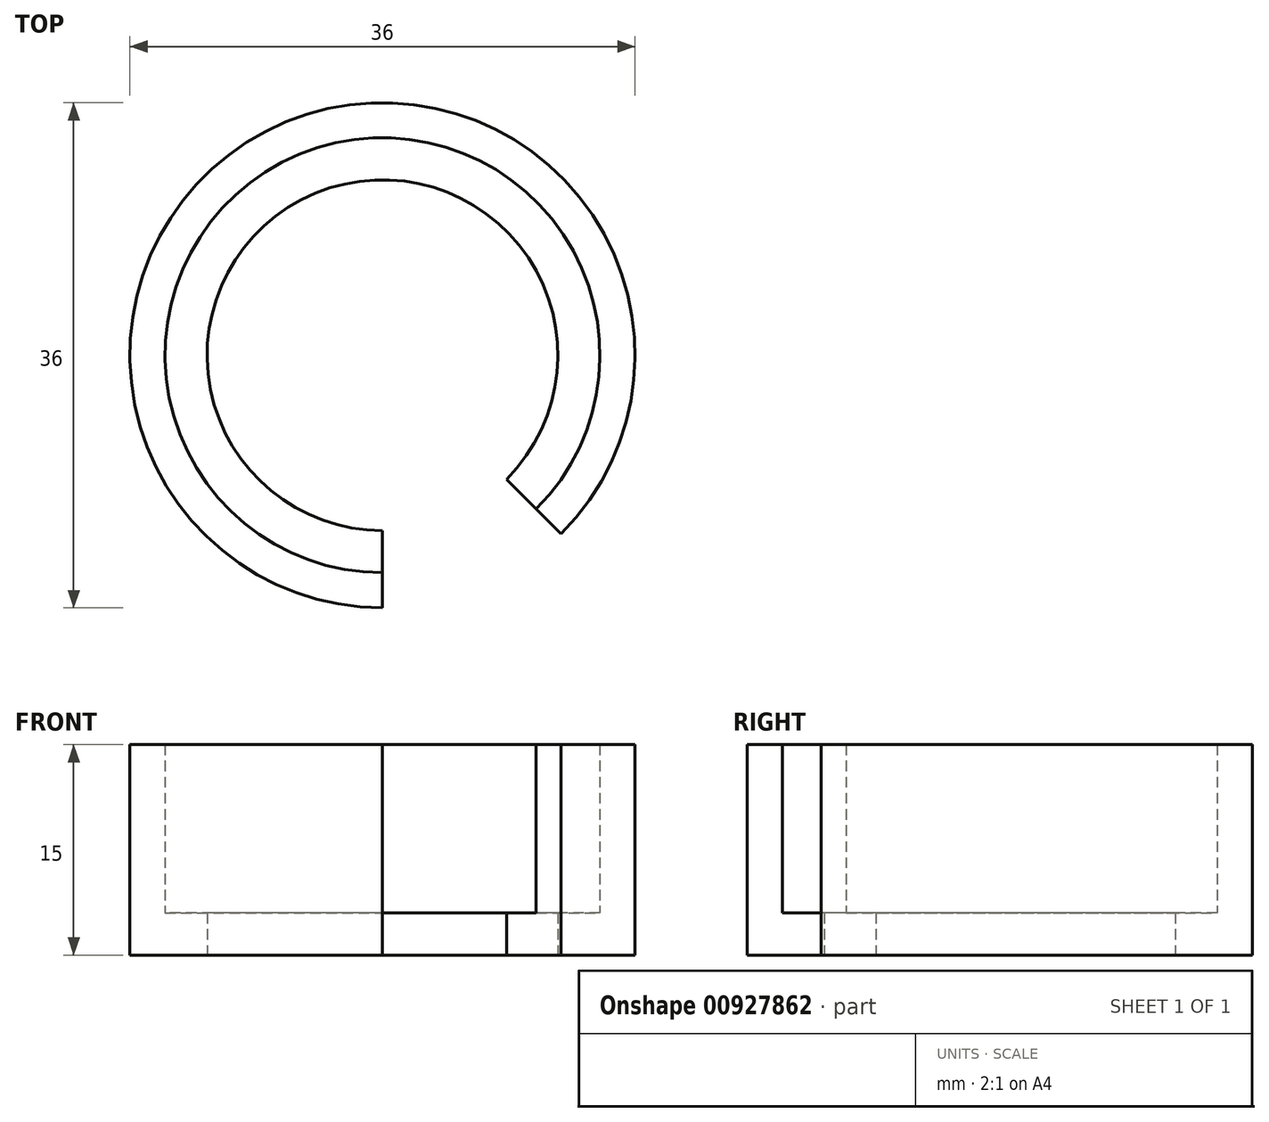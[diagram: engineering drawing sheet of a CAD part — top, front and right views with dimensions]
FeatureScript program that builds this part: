
annotation { "Feature Type Name" : "Feature", "Feature Type Description" : "" }
export const myFeature = defineFeature(function(context is Context, id is Id, definition is map)
    precondition{}
    {
        {
            var Q0;
            Q0=qCreatedBy(makeId("Top.planeOp"),FACE);
            var sketch = newSketch(context, id + "F0", { "sketchPlane" : qUnion([Q0])});
            skCircle(sketch, "E0", {"center": v(0, 0) * mm, "radius": 12.5 * mm});
            skCircle(sketch, "E1", {"center": v(0, 0) * mm, "radius": 15.5 * mm});
            skCircle(sketch, "E2", {"center": v(0, 0) * mm, "radius": 18 * mm});
            skLineSegment(sketch, "E3", {"start": v(0, 0) * mm, "end": v(0, -18) * mm});
            skLineSegment(sketch, "E4", {"start": v(0, 0) * mm, "end": v(12.73, -12.73) * mm});
            skSolve(sketch);
        }
        {
            var Q0;
            {var subQ0=sQuery(id+"F0.wireOp",EDGE,"E3");var subQ1=sQuery(id+"F0.wireOp",EDGE,"E0");var subQ2=makeQuery(id+"F0.imprint","INTERSECT",VERTEX,{"derivedFrom":[subQ1,subQ0]});Q0=makeQuery(id+"F0.imprint","IMPRINT",FACE,{"disambiguationData":[TD([[makeQuery(id+"F0.imprint","IMPRINT",EDGE,{"disambiguationData":[TD([[subQ2,1.0]])],"derivedFrom":subQ1}),-1.0]])]});}
            extrude(context, id + "F1", {"entities" : qUnion([Q0]), "depth" : 3 * mm, "offsetDistance" : 25 * mm});
        }
        {
            var Q0;
            {var subQ0=sQuery(id+"F0.wireOp",EDGE,"E3");var subQ1=sQuery(id+"F0.wireOp",EDGE,"E1");var subQ2=makeQuery(id+"F0.imprint","INTERSECT",VERTEX,{"derivedFrom":[subQ1,subQ0]});Q0=makeQuery(id+"F0.imprint","IMPRINT",FACE,{"disambiguationData":[TD([[makeQuery(id+"F0.imprint","IMPRINT",EDGE,{"disambiguationData":[TD([[subQ2,1.0]])],"derivedFrom":subQ1}),-1.0]])]});}
            extrude(context, id + "F2", {"entities" : qUnion([Q0]), "operationType" : NewBodyOperationType.ADD, "depth" : 15 * mm, "offsetDistance" : 25 * mm});
        }
    });
